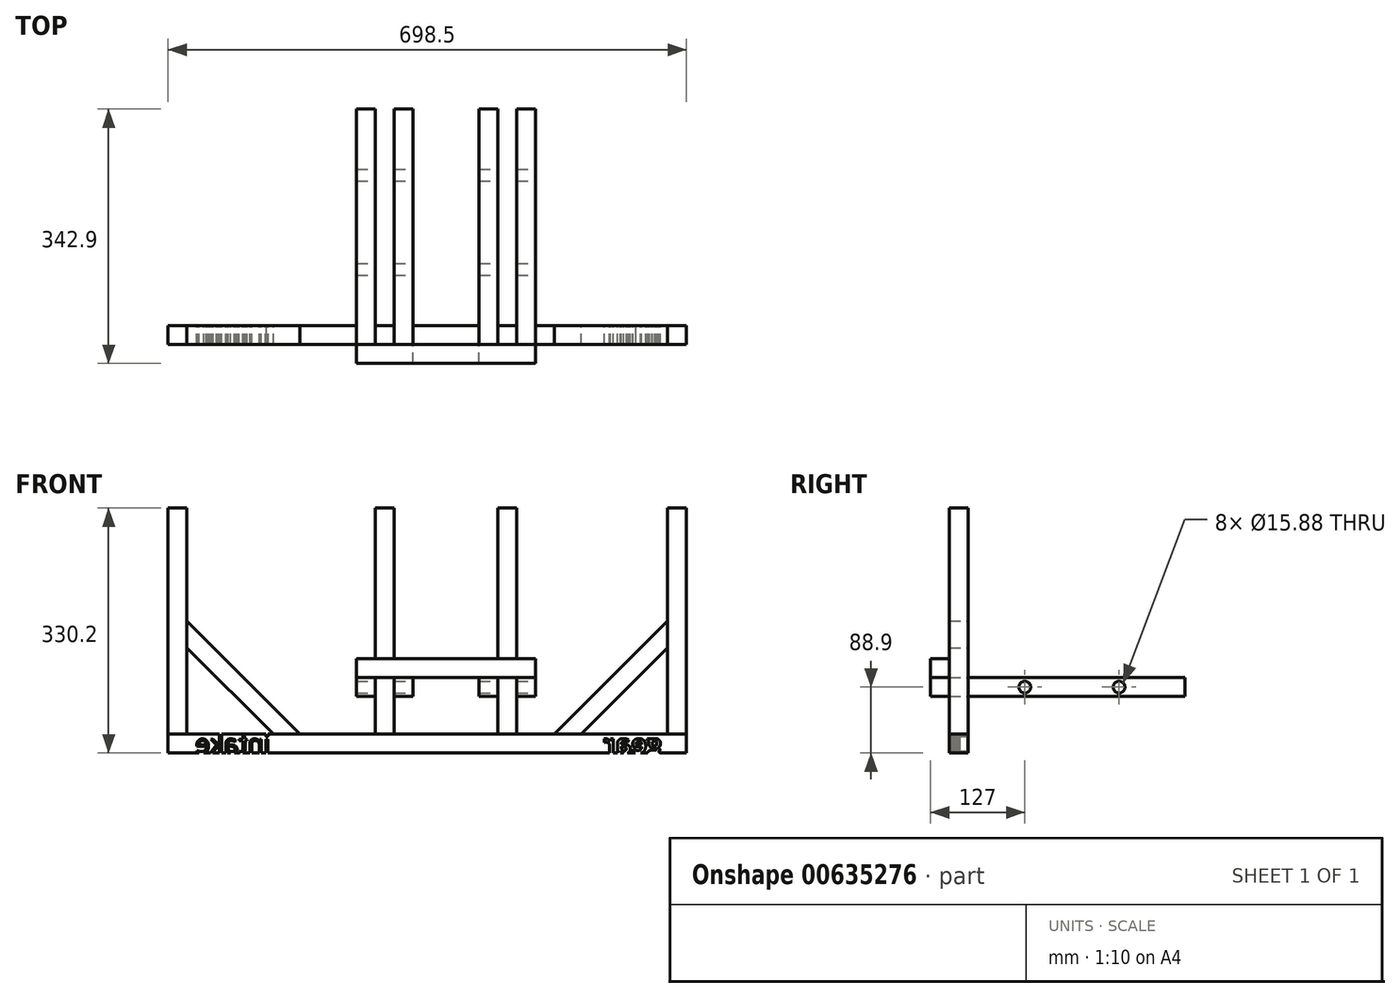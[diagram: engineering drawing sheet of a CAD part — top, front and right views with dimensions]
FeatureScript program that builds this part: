
annotation { "Feature Type Name" : "Feature", "Feature Type Description" : "" }
export const myFeature = defineFeature(function(context is Context, id is Id, definition is map)
    precondition{}
    {
        {
            assignVariable(context, id + "F0", {"name" : "beamLength", "anyValue" : 304.8 * mm});
        }
        {
            assignVariable(context, id + "F1", {"name" : "framePieceLength", "anyValue" : 304.8 * mm});
        }
        {
            assignVariable(context, id + "F2", {"name" : "alumEdge", "anyValue" : 25.4 * mm});
        }
        {
            var Q0;
            Q0=qCreatedBy(makeId("Top.planeOp"),FACE);
            var sketch = newSketch(context, id + "F3", { "sketchPlane" : qUnion([Q0])});
            skLineSegment(sketch, "E0.bottom", {"start": v(-349.25, 12.7) * mm, "end": v(-323.85, 12.7) * mm});
            skLineSegment(sketch, "E0.top", {"start": v(-349.25, -12.7) * mm, "end": v(-323.85, -12.7) * mm});
            skLineSegment(sketch, "E0.left", {"start": v(-349.25, 12.7) * mm, "end": v(-349.25, -12.7) * mm});
            skLineSegment(sketch, "E0.right", {"start": v(-323.85, 12.7) * mm, "end": v(-323.85, -12.7) * mm});
            skPoint(sketch, "E0.middle", {"position": v(-336.55, 0) * mm});
            skLineSegment(sketch, "E1.bottom", {"start": v(349.25, 12.7) * mm, "end": v(323.85, 12.7) * mm});
            skLineSegment(sketch, "E1.top", {"start": v(349.25, -12.7) * mm, "end": v(323.85, -12.7) * mm});
            skLineSegment(sketch, "E1.left", {"start": v(349.25, 12.7) * mm, "end": v(349.25, -12.7) * mm});
            skLineSegment(sketch, "E1.right", {"start": v(323.85, 12.7) * mm, "end": v(323.85, -12.7) * mm});
            skPoint(sketch, "E1.middle", {"position": v(336.55, 0) * mm});
            skLineSegment(sketch, "E2", {"start": v(-349.25, 0) * mm, "end": v(349.25, 0) * mm, "construction": true});
            skLineSegment(sketch, "E3.bottom", {"start": v(120.65, 12.7) * mm, "end": v(95.25, 12.7) * mm});
            skLineSegment(sketch, "E3.top", {"start": v(120.65, -12.7) * mm, "end": v(95.25, -12.7) * mm});
            skLineSegment(sketch, "E3.left", {"start": v(120.65, 12.7) * mm, "end": v(120.65, -12.7) * mm});
            skLineSegment(sketch, "E3.right", {"start": v(95.25, 12.7) * mm, "end": v(95.25, -12.7) * mm});
            skPoint(sketch, "E3.middle", {"position": v(107.95, 0) * mm});
            skLineSegment(sketch, "E4.bottom", {"start": v(-44.45, 12.7) * mm, "end": v(-69.85, 12.7) * mm});
            skLineSegment(sketch, "E4.top", {"start": v(-44.45, -12.7) * mm, "end": v(-69.85, -12.7) * mm});
            skLineSegment(sketch, "E4.left", {"start": v(-44.45, 12.7) * mm, "end": v(-44.45, -12.7) * mm});
            skLineSegment(sketch, "E4.right", {"start": v(-69.85, 12.7) * mm, "end": v(-69.85, -12.7) * mm});
            skPoint(sketch, "E4.middle", {"position": v(-57.15, 0) * mm});
            skPoint(sketch, "E4.cornerSnap0", {"position": v(107.95, 12.7) * mm});
            skSolve(sketch);
        }
        {
            var Q0;
            Q0=makeQuery(id+"F3.imprint","IMPRINT",FACE,{"disambiguationData":[TD([[makeQuery(id+"F3.imprint","IMPRINT",EDGE,{"derivedFrom":sQuery(id+"F3.wireOp",EDGE,"E0.bottom")}),-1.0]])]});
            var Q1;
            Q1=makeQuery(id+"F3.imprint","IMPRINT",FACE,{"disambiguationData":[TD([[makeQuery(id+"F3.imprint","IMPRINT",EDGE,{"derivedFrom":sQuery(id+"F3.wireOp",EDGE,"E4.bottom")}),1.0]])]});
            var Q2;
            Q2=makeQuery(id+"F3.imprint","IMPRINT",FACE,{"disambiguationData":[TD([[makeQuery(id+"F3.imprint","IMPRINT",EDGE,{"derivedFrom":sQuery(id+"F3.wireOp",EDGE,"E3.bottom")}),1.0]])]});
            var Q3;
            Q3=makeQuery(id+"F3.imprint","IMPRINT",FACE,{"disambiguationData":[TD([[makeQuery(id+"F3.imprint","IMPRINT",EDGE,{"derivedFrom":sQuery(id+"F3.wireOp",EDGE,"E1.bottom")}),1.0]])]});
            extrude(context, id + "F4", {"entities" : qUnion([Q0, Q1, Q2, Q3]), "depth" : getVariable(context, 'framePieceLength'), "offsetDistance" : 25 * mm});
        }
        {
            var Q0;
            Q0=qCreatedBy(makeId("Front.planeOp"),FACE);
            var sketch = newSketch(context, id + "F5", { "sketchPlane" : qUnion([Q0])});
            skLineSegment(sketch, "E5.bottom", {"start": v(349.25, 0) * mm, "end": v(-349.25, 0) * mm});
            skLineSegment(sketch, "E5.top", {"start": v(349.25, -25.4) * mm, "end": v(-349.25, -25.4) * mm});
            skLineSegment(sketch, "E5.left", {"start": v(349.25, 0) * mm, "end": v(349.25, -25.4) * mm});
            skLineSegment(sketch, "E5.right", {"start": v(-349.25, 0) * mm, "end": v(-349.25, -25.4) * mm});
            skSolve(sketch);
        }
        {
            var Q0;
            Q0=makeQuery(id+"F5.imprint","IMPRINT",FACE,{"disambiguationData":[TD([[makeQuery(id+"F5.imprint","IMPRINT",EDGE,{"derivedFrom":sQuery(id+"F5.wireOp",EDGE,"E5.bottom")}),1.0]])]});
            extrude(context, id + "F6", {"entities" : qUnion([Q0]), "depth" : getVariable(context, 'alumEdge'), "offsetDistance" : 25 * mm, "symmetric" : true});
        }
        {
            var Q0;
            Q0=makeQuery(id+"F6.opExtrude","CAP_FACE",FACE,{"disambiguationData":[OSD([sQuery(id+"F5.wireOp",EDGE,"E5.bottom"),sQuery(id+"F5.wireOp",EDGE,"E5.top"),sQuery(id+"F5.wireOp",EDGE,"E5.left"),sQuery(id+"F5.wireOp",EDGE,"E5.right")])],"isStart":true});
            var sketch = newSketch(context, id + "F7", { "sketchPlane" : qUnion([Q0])});
            skText(sketch, "E6", { "text": "gear", "fontName": "OpenSans-Bold.ttf"});
            skText(sketch, "E7", { "text": "intake", "fontName": "OpenSans-Regular.ttf"});
            const initialGuessF7  = {"E6": [-0.31566, -0.0254, 1, 0, 0.0254], "E7": [0.21161, -0.0254, 1, 0, 0.0254]};
            skSetInitialGuess(sketch, initialGuessF7);
            skSolve(sketch);
        }
        {
            var Q0;
            Q0=qSketchRegion(id+"F7",true);
            extrude(context, id + "F8", {"entities" : qUnion([Q0]), "operationType" : NewBodyOperationType.REMOVE, "endBound" : BoundingType.THROUGH_ALL, "oppositeDirection" : true, "depth" : getVariable(context, 'alumEdge'), "offsetDistance" : 25 * mm});
        }
        {
            var Q0;
            Q0=qCreatedBy(makeId("Front.planeOp"),FACE);
            var sketch = newSketch(context, id + "F9", { "sketchPlane" : qUnion([Q0])});
            skLineSegment(sketch, "E8", {"start": v(349.25, 8.04) * mm, "end": v(171.45, 8.04) * mm, "construction": true});
            skLineSegment(sketch, "E9", {"start": v(171.45, 0) * mm, "end": v(323.85, 152.4) * mm});
            skLineSegment(sketch, "E10", {"start": v(311.93, 152.4) * mm, "end": v(311.93, -25.4) * mm, "construction": true});
            skLineSegment(sketch, "E11", {"start": v(311.93, 152.4) * mm, "end": v(335.77, 152.4) * mm, "construction": true});
            skPoint(sketch, "E12", {"position": v(323.85, 152.4) * mm});
            skLineSegment(sketch, "E13", {"start": v(207.37, 0) * mm, "end": v(323.85, 116.48) * mm});
            skLineSegment(sketch, "E14", {"start": v(-349.25, 9.12) * mm, "end": v(-171.45, 9.12) * mm, "construction": true});
            skLineSegment(sketch, "E15", {"start": v(-315.1, 152.4) * mm, "end": v(-315.1, -25.4) * mm, "construction": true});
            skLineSegment(sketch, "E16", {"start": v(-171.45, 0) * mm, "end": v(-323.85, 152.4) * mm});
            skLineSegment(sketch, "E17", {"start": v(-323.85, 116.48) * mm, "end": v(-207.37, 0) * mm});
            skLineSegment(sketch, "E18", {"start": v(-323.85, 152.4) * mm, "end": v(-323.85, 116.48) * mm});
            skLineSegment(sketch, "E19", {"start": v(-207.37, 0) * mm, "end": v(-171.45, 0) * mm});
            skLineSegment(sketch, "E20", {"start": v(207.37, 0) * mm, "end": v(171.45, 0) * mm});
            skLineSegment(sketch, "E21", {"start": v(323.85, 152.4) * mm, "end": v(323.85, 116.48) * mm});
            skSolve(sketch);
        }
        {
            var Q0;
            Q0=qSketchRegion(id+"F9",true);
            extrude(context, id + "F10", {"entities" : qUnion([Q0]), "depth" : getVariable(context, 'alumEdge'), "offsetDistance" : 25 * mm, "symmetric" : true});
        }
        {
            var Q0;
            Q0=qCreatedBy(makeId("Front.planeOp"),FACE);
            var sketch = newSketch(context, id + "F11", { "sketchPlane" : qUnion([Q0])});
            skLineSegment(sketch, "E22", {"start": v(164.46, 50.8) * mm, "end": v(-93.34, 50.8) * mm, "construction": true});
            skLineSegment(sketch, "E23.bottom", {"start": v(120.65, 50.8) * mm, "end": v(146.05, 50.8) * mm});
            skLineSegment(sketch, "E23.top", {"start": v(120.65, 76.2) * mm, "end": v(146.05, 76.2) * mm});
            skLineSegment(sketch, "E23.left", {"start": v(120.65, 50.8) * mm, "end": v(120.65, 76.2) * mm});
            skLineSegment(sketch, "E23.right", {"start": v(146.05, 50.8) * mm, "end": v(146.05, 76.2) * mm});
            skLineSegment(sketch, "E24.bottom", {"start": v(95.25, 50.8) * mm, "end": v(69.85, 50.8) * mm});
            skLineSegment(sketch, "E24.top", {"start": v(95.25, 76.2) * mm, "end": v(69.85, 76.2) * mm});
            skLineSegment(sketch, "E24.left", {"start": v(95.25, 50.8) * mm, "end": v(95.25, 76.2) * mm});
            skLineSegment(sketch, "E24.right", {"start": v(69.85, 50.8) * mm, "end": v(69.85, 76.2) * mm});
            skLineSegment(sketch, "E25.bottom", {"start": v(-44.45, 50.8) * mm, "end": v(-19.05, 50.8) * mm});
            skLineSegment(sketch, "E25.top", {"start": v(-44.45, 76.2) * mm, "end": v(-19.05, 76.2) * mm});
            skLineSegment(sketch, "E25.left", {"start": v(-44.45, 50.8) * mm, "end": v(-44.45, 76.2) * mm});
            skLineSegment(sketch, "E25.right", {"start": v(-19.05, 50.8) * mm, "end": v(-19.05, 76.2) * mm});
            skLineSegment(sketch, "E26.bottom", {"start": v(-69.85, 50.8) * mm, "end": v(-95.25, 50.8) * mm});
            skLineSegment(sketch, "E26.top", {"start": v(-69.85, 76.2) * mm, "end": v(-95.25, 76.2) * mm});
            skLineSegment(sketch, "E26.left", {"start": v(-69.85, 50.8) * mm, "end": v(-69.85, 76.2) * mm});
            skLineSegment(sketch, "E26.right", {"start": v(-95.25, 50.8) * mm, "end": v(-95.25, 76.2) * mm});
            skSolve(sketch);
        }
        {
            var Q0;
            Q0=makeQuery(id+"F11.imprint","IMPRINT",FACE,{"disambiguationData":[TD([[makeQuery(id+"F11.imprint","IMPRINT",EDGE,{"derivedFrom":sQuery(id+"F11.wireOp",EDGE,"E23.bottom")}),1.0]])]});
            var Q1;
            Q1=makeQuery(id+"F11.imprint","IMPRINT",FACE,{"disambiguationData":[TD([[makeQuery(id+"F11.imprint","IMPRINT",EDGE,{"derivedFrom":sQuery(id+"F11.wireOp",EDGE,"E24.bottom")}),-1.0]])]});
            var Q2;
            Q2=makeQuery(id+"F11.imprint","IMPRINT",FACE,{"disambiguationData":[TD([[makeQuery(id+"F11.imprint","IMPRINT",EDGE,{"derivedFrom":sQuery(id+"F11.wireOp",EDGE,"E25.bottom")}),1.0]])]});
            var Q3;
            Q3=makeQuery(id+"F11.imprint","IMPRINT",FACE,{"disambiguationData":[TD([[makeQuery(id+"F11.imprint","IMPRINT",EDGE,{"derivedFrom":sQuery(id+"F11.wireOp",EDGE,"E26.bottom")}),-1.0]])]});
            var Q4;
            Q4=qConstructionFilter(qBodyType(qCreatedBy(id+"F11",EDGE),BodyType.WIRE),ConstructionObject.NO);
            extrude(context, id + "F12", {"entities" : qUnion([Q0, Q1, Q2, Q3]), "surfaceEntities" : qUnion([Q4]), "depth" : getVariable(context, 'alumEdge') * 1.5, "offsetDistance" : 25 * mm, "hasSecondDirection" : true, "secondDirectionOppositeDirection" : true, "secondDirectionDepth" : getVariable(context, 'beamLength')});
        }
        {
            var Q0;
            Q0=makeQuery(id+"F12.opExtrude","SWEPT_FACE",FACE,{"disambiguationData":[OSD([sQuery(id+"F11.wireOp",EDGE,"E25.top")])]});
            var sketch = newSketch(context, id + "F13", { "sketchPlane" : qUnion([Q0])});
            skLineSegment(sketch, "E27.bottom", {"start": v(-95.25, -12.7) * mm, "end": v(146.05, -12.7) * mm});
            skLineSegment(sketch, "E27.top", {"start": v(-95.25, -38.1) * mm, "end": v(146.05, -38.1) * mm});
            skLineSegment(sketch, "E27.left", {"start": v(-95.25, -12.7) * mm, "end": v(-95.25, -38.1) * mm});
            skLineSegment(sketch, "E27.right", {"start": v(146.05, -12.7) * mm, "end": v(146.05, -38.1) * mm});
            skSolve(sketch);
        }
        {
            var Q0;
            Q0=qSketchRegion(id+"F13",true);
            extrude(context, id + "F14", {"entities" : qUnion([Q0]), "depth" : getVariable(context, 'alumEdge'), "offsetDistance" : 25 * mm});
        }
        {
            var Q0;
            Q0=makeQuery(id+"F12.opExtrude","SWEPT_FACE",FACE,{"disambiguationData":[OSD([sQuery(id+"F11.wireOp",EDGE,"E23.right")])]});
            var sketch = newSketch(context, id + "F15", { "sketchPlane" : qUnion([Q0])});
            skLineSegment(sketch, "E28", {"start": v(12.7, 63.5) * mm, "end": v(215.9, 63.5) * mm, "construction": true});
            skLineSegment(sketch, "E29", {"start": v(75.48, 76.2) * mm, "end": v(75.48, 50.8) * mm, "construction": true});
            skPoint(sketch, "E30", {"position": v(75.48, 63.5) * mm});
            skCircle(sketch, "E31", {"center": v(215.9, 63.5) * mm, "radius": 7.94 * mm});
            skSolve(sketch);
        }
        {
            var Q0;
            Q0=makeQuery(id+"F15.imprint","IMPRINT",FACE,{"disambiguationData":[TD([[makeQuery(id+"F15.imprint","IMPRINT",EDGE,{"derivedFrom":sQuery(id+"F15.wireOp",EDGE,"E31")}),1.0]])]});
            extrude(context, id + "F16", {"entities" : qUnion([Q0]), "operationType" : NewBodyOperationType.REMOVE, "endBound" : BoundingType.THROUGH_ALL, "oppositeDirection" : true, "depth" : 508 * mm, "offsetDistance" : 25 * mm});
        }
        {
            var Q0;
            Q0=makeQuery(id+"F15.imprint","IMPRINT",FACE,{"disambiguationData":[TD([[makeQuery(id+"F15.imprint","IMPRINT",EDGE,{"derivedFrom":sQuery(id+"F15.wireOp",EDGE,"E31")}),-1.0]])]});
            var sketch = newSketch(context, id + "F17", { "sketchPlane" : qUnion([Q0])});
            skLineSegment(sketch, "E32", {"start": v(12.7, 63.5) * mm, "end": v(88.9, 63.5) * mm, "construction": true});
            skCircle(sketch, "E33", {"center": v(88.9, 63.5) * mm, "radius": 7.94 * mm});
            skSolve(sketch);
        }
        {
            var Q0;
            Q0=makeQuery(id+"F17.imprint","IMPRINT",FACE,{"disambiguationData":[TD([[makeQuery(id+"F17.imprint","IMPRINT",EDGE,{"derivedFrom":sQuery(id+"F17.wireOp",EDGE,"E33")}),1.0]])]});
            extrude(context, id + "F18", {"entities" : qUnion([Q0]), "operationType" : NewBodyOperationType.REMOVE, "endBound" : BoundingType.THROUGH_ALL, "oppositeDirection" : true, "depth" : 100 * mm, "offsetDistance" : 25 * mm});
        }
    });
